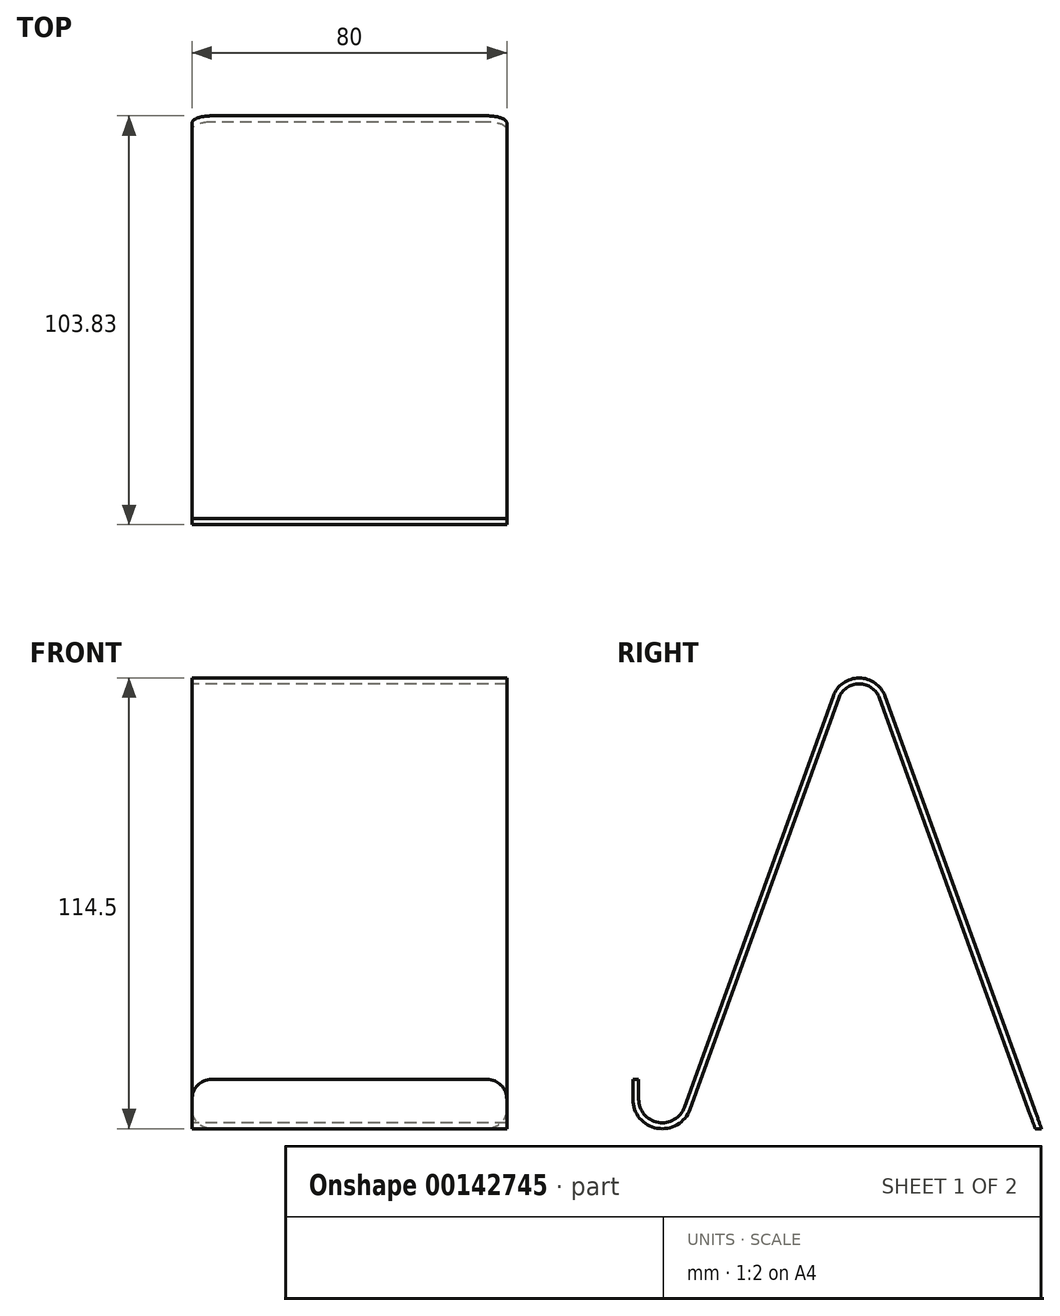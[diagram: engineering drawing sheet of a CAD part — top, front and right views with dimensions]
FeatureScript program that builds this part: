
annotation { "Feature Type Name" : "Feature", "Feature Type Description" : "" }
export const myFeature = defineFeature(function(context is Context, id is Id, definition is map)
    precondition{}
    {
        {
            var Q0;
            Q0=qCreatedBy(makeId("Right.planeOp"),FACE);
            var sketch = newSketch(context, id + "F0", { "sketchPlane" : qUnion([Q0])});
            skArc(sketch, "E0", {"start": v(-7.5, 0) * mm, "mid": v(-1.3, -7.39) * mm, "end": v(7.05, -2.55) * mm});
            skArc(sketch, "E1", {"start": v(55.17, 101.87) * mm, "mid": v(50, 105.5) * mm, "end": v(44.83, 101.87) * mm});
            skLineSegment(sketch, "E2", {"start": v(44.83, 101.87) * mm, "end": v(7.05, -2.55) * mm});
            skLineSegment(sketch, "E3", {"start": v(50, 100) * mm, "end": v(50, 0) * mm, "construction": true});
            skLineSegment(sketch, "E4.MirrorCS", {"start": v(55.17, 101.87) * mm, "end": v(94.74, -7.5) * mm});
            skLineSegment(sketch, "E5", {"start": v(0, -7.5) * mm, "end": v(108.37, -7.5) * mm, "construction": true});
            skLineSegment(sketch, "E6", {"start": v(-7.5, 0) * mm, "end": v(-7.5, 5) * mm});
            skLineSegment(sketch, "E7.0", {"start": v(-6, 0) * mm, "end": v(-6, 5) * mm});
            skLineSegment(sketch, "E7.1", {"start": v(56.58, 102.38) * mm, "end": v(96.33, -7.5) * mm});
            skArc(sketch, "E7.2", {"start": v(56.58, 102.38) * mm, "mid": v(50, 107) * mm, "end": v(43.42, 102.38) * mm});
            skLineSegment(sketch, "E7.3", {"start": v(43.42, 102.38) * mm, "end": v(5.64, -2.04) * mm});
            skArc(sketch, "E7.4", {"start": v(-6, 0) * mm, "mid": v(-1.04, -5.9) * mm, "end": v(5.64, -2.04) * mm});
            skLineSegment(sketch, "E8", {"start": v(94.74, -7.5) * mm, "end": v(96.33, -7.5) * mm});
            skLineSegment(sketch, "E9", {"start": v(-7.5, 5) * mm, "end": v(-6, 5) * mm});
            skSolve(sketch);
        }
        {
            var Q0;
            Q0=makeQuery(id+"F0.imprint","IMPRINT",FACE,{"disambiguationData":[TD([[makeQuery(id+"F0.imprint","IMPRINT",EDGE,{"derivedFrom":sQuery(id+"F0.wireOp",EDGE,"E0")}),1.0]])]});
            extrude(context, id + "F1", {"entities" : qUnion([Q0]), "endBound" : BoundingType.SYMMETRIC, "depth" : 80 * mm});
        }
        {
            var Q0;
            Q0=makeQuery(id+"F1.opExtrude","CAP_EDGE",EDGE,{"disambiguationData":[OSD([sQuery(id+"F0.wireOp",EDGE,"E9")])],"isStart":false});
            var Q1;
            Q1=makeQuery(id+"F1.opExtrude","CAP_EDGE",EDGE,{"disambiguationData":[OSD([sQuery(id+"F0.wireOp",EDGE,"E9")])],"isStart":true});
            var Q2;
            Q2=makeQuery(id+"F1.opExtrude","CAP_EDGE",EDGE,{"disambiguationData":[OSD([sQuery(id+"F0.wireOp",EDGE,"E8")])],"isStart":true});
            var Q3;
            Q3=makeQuery(id+"F1.opExtrude","CAP_EDGE",EDGE,{"disambiguationData":[OSD([sQuery(id+"F0.wireOp",EDGE,"E8")])],"isStart":false});
            fillet(context, id + "F2", {"entities" : qUnion([Q0, Q1, Q2, Q3]), "radius" : 5 * mm, "tangentPropagation" : true, "allowEdgeOverflow" : false});
        }
    });
